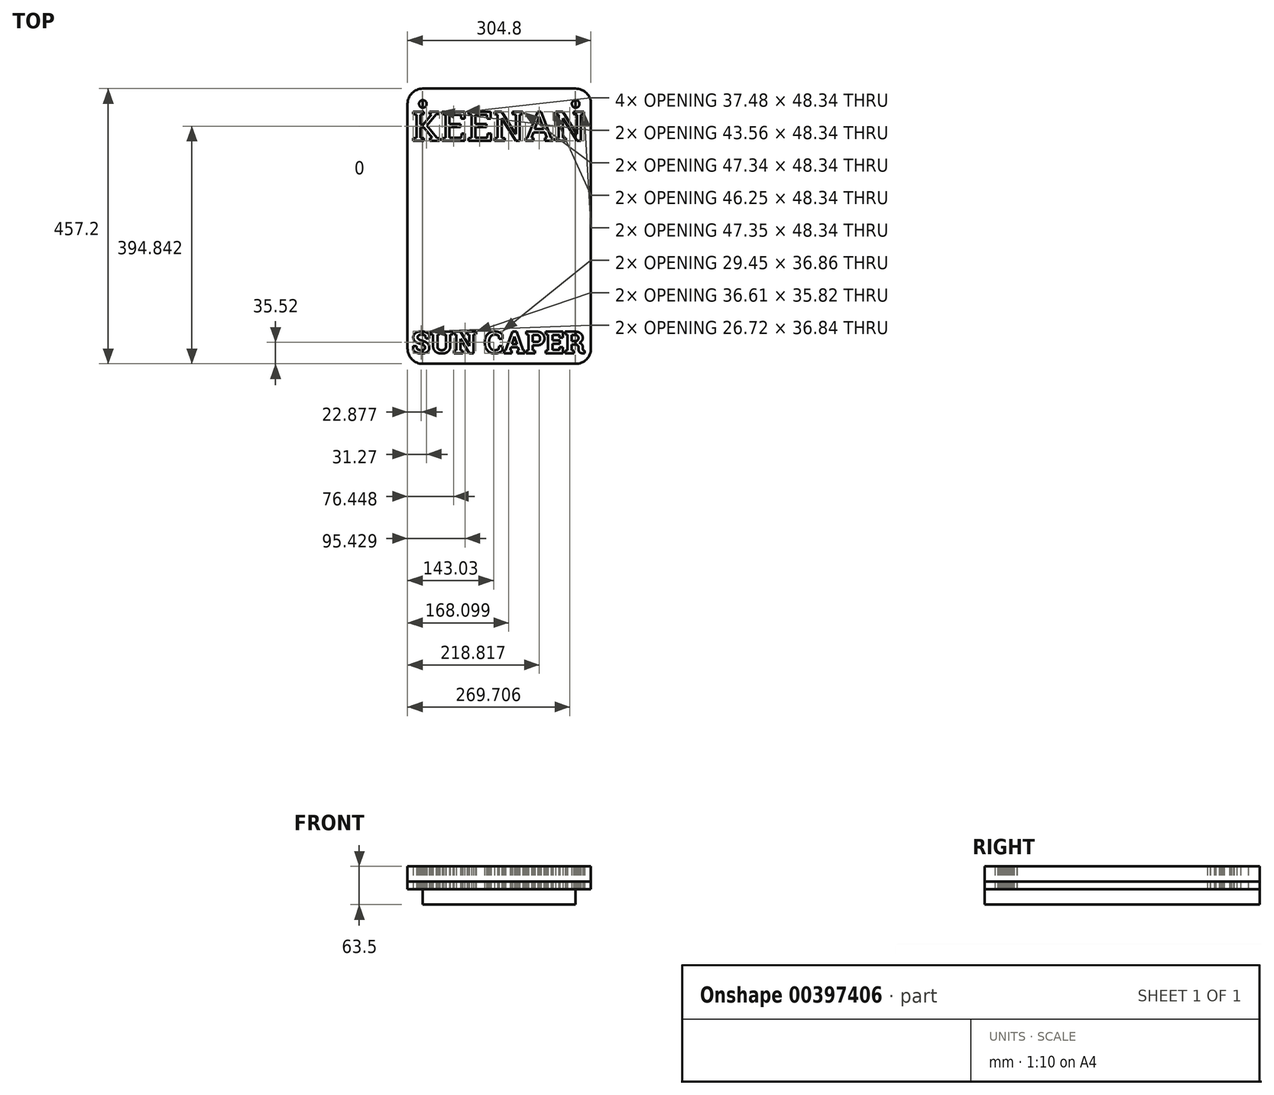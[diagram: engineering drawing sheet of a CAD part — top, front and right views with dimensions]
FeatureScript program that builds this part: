
annotation { "Feature Type Name" : "Feature", "Feature Type Description" : "" }
export const myFeature = defineFeature(function(context is Context, id is Id, definition is map)
    precondition{}
    {
        {
            var Q0;
            Q0=qCreatedBy(makeId("Top.planeOp"),FACE);
            var sketch = newSketch(context, id + "F0", { "sketchPlane" : qUnion([Q0])});
            skLineSegment(sketch, "E0.bottom", {"start": v(25.4, 0) * mm, "end": v(279.4, 0) * mm});
            skLineSegment(sketch, "E0.top", {"start": v(25.4, 457.2) * mm, "end": v(279.4, 457.2) * mm});
            skLineSegment(sketch, "E0.left", {"start": v(0, 25.4) * mm, "end": v(0, 431.8) * mm});
            skLineSegment(sketch, "E0.right", {"start": v(304.8, 25.4) * mm, "end": v(304.8, 431.8) * mm});
            skText(sketch, "E1", { "text": "SUN CAPER", "fontName": "RobotoSlab-Bold.ttf"});
            skText(sketch, "E2", { "text": "KEENAN", "fontName": "RobotoSlab-Regular.ttf"});
            skPoint(sketch, "E3.visualSharp", {"position": v(0, 457.2) * mm});
            skArc(sketch, "E3.filletArc", {"start": v(25.4, 457.2) * mm, "mid": v(7.44, 449.76) * mm, "end": v(0, 431.8) * mm});
            skPoint(sketch, "E4.visualSharp", {"position": v(304.8, 457.2) * mm});
            skArc(sketch, "E4.filletArc", {"start": v(304.8, 431.8) * mm, "mid": v(297.36, 449.76) * mm, "end": v(279.4, 457.2) * mm});
            skPoint(sketch, "E5.visualSharp", {"position": v(304.8, 0) * mm});
            skArc(sketch, "E5.filletArc", {"start": v(279.4, 0) * mm, "mid": v(297.36, 7.44) * mm, "end": v(304.8, 25.4) * mm});
            skPoint(sketch, "E6.visualSharp", {"position": v(0, 0) * mm});
            skArc(sketch, "E6.filletArc", {"start": v(0, 25.4) * mm, "mid": v(7.44, 7.44) * mm, "end": v(25.4, 0) * mm});
            skCircle(sketch, "E7", {"center": v(25.4, 431.8) * mm, "radius": 6.35 * mm});
            skCircle(sketch, "E8", {"center": v(279.4, 431.8) * mm, "radius": 6.35 * mm});
            const initialGuessF0  = {"E1": [0.00713, 0.01762, 1, 0, 0.03628], "E2": [0.00713, 0.37067, 1, 0, 0.04896]};
            skSetInitialGuess(sketch, initialGuessF0);
            skSolve(sketch);
        }
        {
            var Q0;
            Q0=makeQuery(id+"F0.imprint","IMPRINT",FACE,{"disambiguationData":[TD([[makeQuery(id+"F0.imprint","IMPRINT",EDGE,{"derivedFrom":sQuery(id+"F0.wireOp",EDGE,"E0.bottom")}),1.0]])]});
            var Q1;
            Q1=makeQuery(id+"F0.imprint","IMPRINT",FACE,{"disambiguationData":[TD([[makeQuery(id+"F0.imprint","IMPRINT",EDGE,{"derivedFrom":sQuery(id+"F0.wireOp",EDGE,"E2.sketch_text.stroke-109")}),1.0]])]});
            var Q2;
            Q2=makeQuery(id+"F0.imprint","IMPRINT",FACE,{"disambiguationData":[TD([[makeQuery(id+"F0.imprint","IMPRINT",EDGE,{"derivedFrom":sQuery(id+"F0.wireOp",EDGE,"E1.sketch_text.stroke-195")}),1.0]])]});
            var Q3;
            Q3=makeQuery(id+"F0.imprint","IMPRINT",FACE,{"disambiguationData":[TD([[makeQuery(id+"F0.imprint","IMPRINT",EDGE,{"derivedFrom":sQuery(id+"F0.wireOp",EDGE,"E1.sketch_text.stroke-138")}),1.0]])]});
            var Q4;
            Q4=makeQuery(id+"F0.imprint","IMPRINT",FACE,{"disambiguationData":[TD([[makeQuery(id+"F0.imprint","IMPRINT",EDGE,{"derivedFrom":sQuery(id+"F0.wireOp",EDGE,"E1.sketch_text.stroke-118")}),1.0]])]});
            extrude(context, id + "F1", {"entities" : qUnion([Q0, Q1, Q2, Q3, Q4]), "depth" : 25.4 * mm});
        }
        {
            var Q0;
            Q0=makeQuery(id+"F1.opExtrude","CAP_FACE",FACE,{"disambiguationData":[OSD([sQuery(id+"F0.wireOp",EDGE,"E0.bottom"),sQuery(id+"F0.wireOp",EDGE,"E0.top"),sQuery(id+"F0.wireOp",EDGE,"E0.left"),sQuery(id+"F0.wireOp",EDGE,"E0.right"),sQuery(id+"F0.wireOp",EDGE,"E1.sketch_text.stroke-0"),sQuery(id+"F0.wireOp",EDGE,"E1.sketch_text.stroke-1"),sQuery(id+"F0.wireOp",EDGE,"E1.sketch_text.stroke-2"),sQuery(id+"F0.wireOp",EDGE,"E1.sketch_text.stroke-3"),sQuery(id+"F0.wireOp",EDGE,"E1.sketch_text.stroke-4"),sQuery(id+"F0.wireOp",EDGE,"E1.sketch_text.stroke-5"),sQuery(id+"F0.wireOp",EDGE,"E1.sketch_text.stroke-6"),sQuery(id+"F0.wireOp",EDGE,"E1.sketch_text.stroke-7"),sQuery(id+"F0.wireOp",EDGE,"E1.sketch_text.stroke-8"),sQuery(id+"F0.wireOp",EDGE,"E1.sketch_text.stroke-9"),sQuery(id+"F0.wireOp",EDGE,"E1.sketch_text.stroke-10"),sQuery(id+"F0.wireOp",EDGE,"E1.sketch_text.stroke-11"),sQuery(id+"F0.wireOp",EDGE,"E1.sketch_text.stroke-12"),sQuery(id+"F0.wireOp",EDGE,"E1.sketch_text.stroke-13"),sQuery(id+"F0.wireOp",EDGE,"E1.sketch_text.stroke-14"),sQuery(id+"F0.wireOp",EDGE,"E1.sketch_text.stroke-15"),sQuery(id+"F0.wireOp",EDGE,"E1.sketch_text.stroke-16"),sQuery(id+"F0.wireOp",EDGE,"E1.sketch_text.stroke-17"),sQuery(id+"F0.wireOp",EDGE,"E1.sketch_text.stroke-18"),sQuery(id+"F0.wireOp",EDGE,"E1.sketch_text.stroke-19"),sQuery(id+"F0.wireOp",EDGE,"E1.sketch_text.stroke-20"),sQuery(id+"F0.wireOp",EDGE,"E1.sketch_text.stroke-21"),sQuery(id+"F0.wireOp",EDGE,"E1.sketch_text.stroke-22"),sQuery(id+"F0.wireOp",EDGE,"E1.sketch_text.stroke-23"),sQuery(id+"F0.wireOp",EDGE,"E1.sketch_text.stroke-24"),sQuery(id+"F0.wireOp",EDGE,"E1.sketch_text.stroke-25"),sQuery(id+"F0.wireOp",EDGE,"E1.sketch_text.stroke-26"),sQuery(id+"F0.wireOp",EDGE,"E1.sketch_text.stroke-27"),sQuery(id+"F0.wireOp",EDGE,"E1.sketch_text.stroke-28"),sQuery(id+"F0.wireOp",EDGE,"E1.sketch_text.stroke-29"),sQuery(id+"F0.wireOp",EDGE,"E1.sketch_text.stroke-30"),sQuery(id+"F0.wireOp",EDGE,"E1.sketch_text.stroke-31"),sQuery(id+"F0.wireOp",EDGE,"E1.sketch_text.stroke-32"),sQuery(id+"F0.wireOp",EDGE,"E1.sketch_text.stroke-33"),sQuery(id+"F0.wireOp",EDGE,"E1.sketch_text.stroke-34"),sQuery(id+"F0.wireOp",EDGE,"E1.sketch_text.stroke-35"),sQuery(id+"F0.wireOp",EDGE,"E1.sketch_text.stroke-36"),sQuery(id+"F0.wireOp",EDGE,"E1.sketch_text.stroke-37"),sQuery(id+"F0.wireOp",EDGE,"E1.sketch_text.stroke-38"),sQuery(id+"F0.wireOp",EDGE,"E1.sketch_text.stroke-39"),sQuery(id+"F0.wireOp",EDGE,"E1.sketch_text.stroke-40"),sQuery(id+"F0.wireOp",EDGE,"E1.sketch_text.stroke-41"),sQuery(id+"F0.wireOp",EDGE,"E1.sketch_text.stroke-42"),sQuery(id+"F0.wireOp",EDGE,"E1.sketch_text.stroke-43"),sQuery(id+"F0.wireOp",EDGE,"E1.sketch_text.stroke-44"),sQuery(id+"F0.wireOp",EDGE,"E1.sketch_text.stroke-45"),sQuery(id+"F0.wireOp",EDGE,"E1.sketch_text.stroke-46"),sQuery(id+"F0.wireOp",EDGE,"E1.sketch_text.stroke-47"),sQuery(id+"F0.wireOp",EDGE,"E1.sketch_text.stroke-48"),sQuery(id+"F0.wireOp",EDGE,"E1.sketch_text.stroke-49"),sQuery(id+"F0.wireOp",EDGE,"E1.sketch_text.stroke-50"),sQuery(id+"F0.wireOp",EDGE,"E1.sketch_text.stroke-51"),sQuery(id+"F0.wireOp",EDGE,"E1.sketch_text.stroke-52"),sQuery(id+"F0.wireOp",EDGE,"E1.sketch_text.stroke-53"),sQuery(id+"F0.wireOp",EDGE,"E1.sketch_text.stroke-54"),sQuery(id+"F0.wireOp",EDGE,"E1.sketch_text.stroke-55"),sQuery(id+"F0.wireOp",EDGE,"E1.sketch_text.stroke-56"),sQuery(id+"F0.wireOp",EDGE,"E1.sketch_text.stroke-57"),sQuery(id+"F0.wireOp",EDGE,"E1.sketch_text.stroke-58"),sQuery(id+"F0.wireOp",EDGE,"E1.sketch_text.stroke-59"),sQuery(id+"F0.wireOp",EDGE,"E1.sketch_text.stroke-60"),sQuery(id+"F0.wireOp",EDGE,"E1.sketch_text.stroke-61"),sQuery(id+"F0.wireOp",EDGE,"E1.sketch_text.stroke-62"),sQuery(id+"F0.wireOp",EDGE,"E1.sketch_text.stroke-63"),sQuery(id+"F0.wireOp",EDGE,"E1.sketch_text.stroke-64"),sQuery(id+"F0.wireOp",EDGE,"E1.sketch_text.stroke-65"),sQuery(id+"F0.wireOp",EDGE,"E1.sketch_text.stroke-66"),sQuery(id+"F0.wireOp",EDGE,"E1.sketch_text.stroke-67"),sQuery(id+"F0.wireOp",EDGE,"E1.sketch_text.stroke-68"),sQuery(id+"F0.wireOp",EDGE,"E1.sketch_text.stroke-69"),sQuery(id+"F0.wireOp",EDGE,"E1.sketch_text.stroke-70"),sQuery(id+"F0.wireOp",EDGE,"E1.sketch_text.stroke-71"),sQuery(id+"F0.wireOp",EDGE,"E1.sketch_text.stroke-72"),sQuery(id+"F0.wireOp",EDGE,"E1.sketch_text.stroke-73"),sQuery(id+"F0.wireOp",EDGE,"E1.sketch_text.stroke-74"),sQuery(id+"F0.wireOp",EDGE,"E1.sketch_text.stroke-75"),sQuery(id+"F0.wireOp",EDGE,"E1.sketch_text.stroke-76"),sQuery(id+"F0.wireOp",EDGE,"E1.sketch_text.stroke-77"),sQuery(id+"F0.wireOp",EDGE,"E1.sketch_text.stroke-78"),sQuery(id+"F0.wireOp",EDGE,"E1.sketch_text.stroke-79"),sQuery(id+"F0.wireOp",EDGE,"E1.sketch_text.stroke-80"),sQuery(id+"F0.wireOp",EDGE,"E1.sketch_text.stroke-81"),sQuery(id+"F0.wireOp",EDGE,"E1.sketch_text.stroke-82"),sQuery(id+"F0.wireOp",EDGE,"E1.sketch_text.stroke-83"),sQuery(id+"F0.wireOp",EDGE,"E1.sketch_text.stroke-84"),sQuery(id+"F0.wireOp",EDGE,"E1.sketch_text.stroke-85"),sQuery(id+"F0.wireOp",EDGE,"E1.sketch_text.stroke-86"),sQuery(id+"F0.wireOp",EDGE,"E1.sketch_text.stroke-87"),sQuery(id+"F0.wireOp",EDGE,"E1.sketch_text.stroke-88"),sQuery(id+"F0.wireOp",EDGE,"E1.sketch_text.stroke-89"),sQuery(id+"F0.wireOp",EDGE,"E1.sketch_text.stroke-90"),sQuery(id+"F0.wireOp",EDGE,"E1.sketch_text.stroke-91"),sQuery(id+"F0.wireOp",EDGE,"E1.sketch_text.stroke-92"),sQuery(id+"F0.wireOp",EDGE,"E1.sketch_text.stroke-93"),sQuery(id+"F0.wireOp",EDGE,"E1.sketch_text.stroke-94"),sQuery(id+"F0.wireOp",EDGE,"E1.sketch_text.stroke-95"),sQuery(id+"F0.wireOp",EDGE,"E1.sketch_text.stroke-96"),sQuery(id+"F0.wireOp",EDGE,"E1.sketch_text.stroke-97"),sQuery(id+"F0.wireOp",EDGE,"E1.sketch_text.stroke-98"),sQuery(id+"F0.wireOp",EDGE,"E1.sketch_text.stroke-99"),sQuery(id+"F0.wireOp",EDGE,"E1.sketch_text.stroke-100"),sQuery(id+"F0.wireOp",EDGE,"E1.sketch_text.stroke-101"),sQuery(id+"F0.wireOp",EDGE,"E1.sketch_text.stroke-102"),sQuery(id+"F0.wireOp",EDGE,"E1.sketch_text.stroke-103"),sQuery(id+"F0.wireOp",EDGE,"E1.sketch_text.stroke-104"),sQuery(id+"F0.wireOp",EDGE,"E1.sketch_text.stroke-105"),sQuery(id+"F0.wireOp",EDGE,"E1.sketch_text.stroke-106"),sQuery(id+"F0.wireOp",EDGE,"E1.sketch_text.stroke-107"),sQuery(id+"F0.wireOp",EDGE,"E1.sketch_text.stroke-108"),sQuery(id+"F0.wireOp",EDGE,"E1.sketch_text.stroke-109"),sQuery(id+"F0.wireOp",EDGE,"E1.sketch_text.stroke-110"),sQuery(id+"F0.wireOp",EDGE,"E1.sketch_text.stroke-111"),sQuery(id+"F0.wireOp",EDGE,"E1.sketch_text.stroke-112"),sQuery(id+"F0.wireOp",EDGE,"E1.sketch_text.stroke-113"),sQuery(id+"F0.wireOp",EDGE,"E1.sketch_text.stroke-114"),sQuery(id+"F0.wireOp",EDGE,"E1.sketch_text.stroke-115"),sQuery(id+"F0.wireOp",EDGE,"E1.sketch_text.stroke-116"),sQuery(id+"F0.wireOp",EDGE,"E1.sketch_text.stroke-117"),sQuery(id+"F0.wireOp",EDGE,"E1.sketch_text.stroke-122"),sQuery(id+"F0.wireOp",EDGE,"E1.sketch_text.stroke-123"),sQuery(id+"F0.wireOp",EDGE,"E1.sketch_text.stroke-124"),sQuery(id+"F0.wireOp",EDGE,"E1.sketch_text.stroke-125"),sQuery(id+"F0.wireOp",EDGE,"E1.sketch_text.stroke-126"),sQuery(id+"F0.wireOp",EDGE,"E1.sketch_text.stroke-127"),sQuery(id+"F0.wireOp",EDGE,"E1.sketch_text.stroke-128"),sQuery(id+"F0.wireOp",EDGE,"E1.sketch_text.stroke-129"),sQuery(id+"F0.wireOp",EDGE,"E1.sketch_text.stroke-130"),sQuery(id+"F0.wireOp",EDGE,"E1.sketch_text.stroke-131"),sQuery(id+"F0.wireOp",EDGE,"E1.sketch_text.stroke-132"),sQuery(id+"F0.wireOp",EDGE,"E1.sketch_text.stroke-133"),sQuery(id+"F0.wireOp",EDGE,"E1.sketch_text.stroke-134"),sQuery(id+"F0.wireOp",EDGE,"E1.sketch_text.stroke-135"),sQuery(id+"F0.wireOp",EDGE,"E1.sketch_text.stroke-136"),sQuery(id+"F0.wireOp",EDGE,"E1.sketch_text.stroke-137"),sQuery(id+"F0.wireOp",EDGE,"E1.sketch_text.stroke-145"),sQuery(id+"F0.wireOp",EDGE,"E1.sketch_text.stroke-146"),sQuery(id+"F0.wireOp",EDGE,"E1.sketch_text.stroke-147"),sQuery(id+"F0.wireOp",EDGE,"E1.sketch_text.stroke-148"),sQuery(id+"F0.wireOp",EDGE,"E1.sketch_text.stroke-149"),sQuery(id+"F0.wireOp",EDGE,"E1.sketch_text.stroke-150"),sQuery(id+"F0.wireOp",EDGE,"E1.sketch_text.stroke-151"),sQuery(id+"F0.wireOp",EDGE,"E1.sketch_text.stroke-152"),sQuery(id+"F0.wireOp",EDGE,"E1.sketch_text.stroke-153"),sQuery(id+"F0.wireOp",EDGE,"E1.sketch_text.stroke-154"),sQuery(id+"F0.wireOp",EDGE,"E1.sketch_text.stroke-155"),sQuery(id+"F0.wireOp",EDGE,"E1.sketch_text.stroke-156"),sQuery(id+"F0.wireOp",EDGE,"E1.sketch_text.stroke-157"),sQuery(id+"F0.wireOp",EDGE,"E1.sketch_text.stroke-158"),sQuery(id+"F0.wireOp",EDGE,"E1.sketch_text.stroke-159"),sQuery(id+"F0.wireOp",EDGE,"E1.sketch_text.stroke-160"),sQuery(id+"F0.wireOp",EDGE,"E1.sketch_text.stroke-161"),sQuery(id+"F0.wireOp",EDGE,"E1.sketch_text.stroke-162"),sQuery(id+"F0.wireOp",EDGE,"E1.sketch_text.stroke-163"),sQuery(id+"F0.wireOp",EDGE,"E1.sketch_text.stroke-164"),sQuery(id+"F0.wireOp",EDGE,"E1.sketch_text.stroke-165"),sQuery(id+"F0.wireOp",EDGE,"E1.sketch_text.stroke-166"),sQuery(id+"F0.wireOp",EDGE,"E1.sketch_text.stroke-167"),sQuery(id+"F0.wireOp",EDGE,"E1.sketch_text.stroke-168"),sQuery(id+"F0.wireOp",EDGE,"E1.sketch_text.stroke-169"),sQuery(id+"F0.wireOp",EDGE,"E1.sketch_text.stroke-170"),sQuery(id+"F0.wireOp",EDGE,"E1.sketch_text.stroke-171"),sQuery(id+"F0.wireOp",EDGE,"E1.sketch_text.stroke-172"),sQuery(id+"F0.wireOp",EDGE,"E1.sketch_text.stroke-173"),sQuery(id+"F0.wireOp",EDGE,"E1.sketch_text.stroke-174"),sQuery(id+"F0.wireOp",EDGE,"E1.sketch_text.stroke-175"),sQuery(id+"F0.wireOp",EDGE,"E1.sketch_text.stroke-176"),sQuery(id+"F0.wireOp",EDGE,"E1.sketch_text.stroke-177"),sQuery(id+"F0.wireOp",EDGE,"E1.sketch_text.stroke-178"),sQuery(id+"F0.wireOp",EDGE,"E1.sketch_text.stroke-179"),sQuery(id+"F0.wireOp",EDGE,"E1.sketch_text.stroke-180"),sQuery(id+"F0.wireOp",EDGE,"E1.sketch_text.stroke-181"),sQuery(id+"F0.wireOp",EDGE,"E1.sketch_text.stroke-182"),sQuery(id+"F0.wireOp",EDGE,"E1.sketch_text.stroke-183"),sQuery(id+"F0.wireOp",EDGE,"E1.sketch_text.stroke-184"),sQuery(id+"F0.wireOp",EDGE,"E1.sketch_text.stroke-185"),sQuery(id+"F0.wireOp",EDGE,"E1.sketch_text.stroke-186"),sQuery(id+"F0.wireOp",EDGE,"E1.sketch_text.stroke-187"),sQuery(id+"F0.wireOp",EDGE,"E1.sketch_text.stroke-188"),sQuery(id+"F0.wireOp",EDGE,"E1.sketch_text.stroke-189"),sQuery(id+"F0.wireOp",EDGE,"E1.sketch_text.stroke-190"),sQuery(id+"F0.wireOp",EDGE,"E1.sketch_text.stroke-191"),sQuery(id+"F0.wireOp",EDGE,"E1.sketch_text.stroke-192"),sQuery(id+"F0.wireOp",EDGE,"E1.sketch_text.stroke-193"),sQuery(id+"F0.wireOp",EDGE,"E1.sketch_text.stroke-194"),sQuery(id+"F0.wireOp",EDGE,"E2.sketch_text.stroke-0"),sQuery(id+"F0.wireOp",EDGE,"E2.sketch_text.stroke-1"),sQuery(id+"F0.wireOp",EDGE,"E2.sketch_text.stroke-2"),sQuery(id+"F0.wireOp",EDGE,"E2.sketch_text.stroke-3"),sQuery(id+"F0.wireOp",EDGE,"E2.sketch_text.stroke-4"),sQuery(id+"F0.wireOp",EDGE,"E2.sketch_text.stroke-5"),sQuery(id+"F0.wireOp",EDGE,"E2.sketch_text.stroke-6"),sQuery(id+"F0.wireOp",EDGE,"E2.sketch_text.stroke-7"),sQuery(id+"F0.wireOp",EDGE,"E2.sketch_text.stroke-8"),sQuery(id+"F0.wireOp",EDGE,"E2.sketch_text.stroke-9"),sQuery(id+"F0.wireOp",EDGE,"E2.sketch_text.stroke-10"),sQuery(id+"F0.wireOp",EDGE,"E2.sketch_text.stroke-11"),sQuery(id+"F0.wireOp",EDGE,"E2.sketch_text.stroke-12"),sQuery(id+"F0.wireOp",EDGE,"E2.sketch_text.stroke-13"),sQuery(id+"F0.wireOp",EDGE,"E2.sketch_text.stroke-14"),sQuery(id+"F0.wireOp",EDGE,"E2.sketch_text.stroke-15"),sQuery(id+"F0.wireOp",EDGE,"E2.sketch_text.stroke-16"),sQuery(id+"F0.wireOp",EDGE,"E2.sketch_text.stroke-17"),sQuery(id+"F0.wireOp",EDGE,"E2.sketch_text.stroke-18"),sQuery(id+"F0.wireOp",EDGE,"E2.sketch_text.stroke-19"),sQuery(id+"F0.wireOp",EDGE,"E2.sketch_text.stroke-20"),sQuery(id+"F0.wireOp",EDGE,"E2.sketch_text.stroke-21"),sQuery(id+"F0.wireOp",EDGE,"E2.sketch_text.stroke-22"),sQuery(id+"F0.wireOp",EDGE,"E2.sketch_text.stroke-23"),sQuery(id+"F0.wireOp",EDGE,"E2.sketch_text.stroke-24"),sQuery(id+"F0.wireOp",EDGE,"E2.sketch_text.stroke-25"),sQuery(id+"F0.wireOp",EDGE,"E2.sketch_text.stroke-26"),sQuery(id+"F0.wireOp",EDGE,"E2.sketch_text.stroke-27"),sQuery(id+"F0.wireOp",EDGE,"E2.sketch_text.stroke-28"),sQuery(id+"F0.wireOp",EDGE,"E2.sketch_text.stroke-29"),sQuery(id+"F0.wireOp",EDGE,"E2.sketch_text.stroke-30"),sQuery(id+"F0.wireOp",EDGE,"E2.sketch_text.stroke-31"),sQuery(id+"F0.wireOp",EDGE,"E2.sketch_text.stroke-32"),sQuery(id+"F0.wireOp",EDGE,"E2.sketch_text.stroke-33"),sQuery(id+"F0.wireOp",EDGE,"E2.sketch_text.stroke-34"),sQuery(id+"F0.wireOp",EDGE,"E2.sketch_text.stroke-35"),sQuery(id+"F0.wireOp",EDGE,"E2.sketch_text.stroke-36"),sQuery(id+"F0.wireOp",EDGE,"E2.sketch_text.stroke-37"),sQuery(id+"F0.wireOp",EDGE,"E2.sketch_text.stroke-38"),sQuery(id+"F0.wireOp",EDGE,"E2.sketch_text.stroke-39"),sQuery(id+"F0.wireOp",EDGE,"E2.sketch_text.stroke-40"),sQuery(id+"F0.wireOp",EDGE,"E2.sketch_text.stroke-41"),sQuery(id+"F0.wireOp",EDGE,"E2.sketch_text.stroke-42"),sQuery(id+"F0.wireOp",EDGE,"E2.sketch_text.stroke-43"),sQuery(id+"F0.wireOp",EDGE,"E2.sketch_text.stroke-44"),sQuery(id+"F0.wireOp",EDGE,"E2.sketch_text.stroke-45"),sQuery(id+"F0.wireOp",EDGE,"E2.sketch_text.stroke-46"),sQuery(id+"F0.wireOp",EDGE,"E2.sketch_text.stroke-47"),sQuery(id+"F0.wireOp",EDGE,"E2.sketch_text.stroke-48"),sQuery(id+"F0.wireOp",EDGE,"E2.sketch_text.stroke-49"),sQuery(id+"F0.wireOp",EDGE,"E2.sketch_text.stroke-50"),sQuery(id+"F0.wireOp",EDGE,"E2.sketch_text.stroke-51"),sQuery(id+"F0.wireOp",EDGE,"E2.sketch_text.stroke-52"),sQuery(id+"F0.wireOp",EDGE,"E2.sketch_text.stroke-53"),sQuery(id+"F0.wireOp",EDGE,"E2.sketch_text.stroke-54"),sQuery(id+"F0.wireOp",EDGE,"E2.sketch_text.stroke-55"),sQuery(id+"F0.wireOp",EDGE,"E2.sketch_text.stroke-56"),sQuery(id+"F0.wireOp",EDGE,"E2.sketch_text.stroke-57"),sQuery(id+"F0.wireOp",EDGE,"E2.sketch_text.stroke-58"),sQuery(id+"F0.wireOp",EDGE,"E2.sketch_text.stroke-59"),sQuery(id+"F0.wireOp",EDGE,"E2.sketch_text.stroke-60"),sQuery(id+"F0.wireOp",EDGE,"E2.sketch_text.stroke-61"),sQuery(id+"F0.wireOp",EDGE,"E2.sketch_text.stroke-62"),sQuery(id+"F0.wireOp",EDGE,"E2.sketch_text.stroke-63"),sQuery(id+"F0.wireOp",EDGE,"E2.sketch_text.stroke-64"),sQuery(id+"F0.wireOp",EDGE,"E2.sketch_text.stroke-65"),sQuery(id+"F0.wireOp",EDGE,"E2.sketch_text.stroke-66"),sQuery(id+"F0.wireOp",EDGE,"E2.sketch_text.stroke-67"),sQuery(id+"F0.wireOp",EDGE,"E2.sketch_text.stroke-68"),sQuery(id+"F0.wireOp",EDGE,"E2.sketch_text.stroke-69"),sQuery(id+"F0.wireOp",EDGE,"E2.sketch_text.stroke-70"),sQuery(id+"F0.wireOp",EDGE,"E2.sketch_text.stroke-71"),sQuery(id+"F0.wireOp",EDGE,"E2.sketch_text.stroke-72"),sQuery(id+"F0.wireOp",EDGE,"E2.sketch_text.stroke-73"),sQuery(id+"F0.wireOp",EDGE,"E2.sketch_text.stroke-74"),sQuery(id+"F0.wireOp",EDGE,"E2.sketch_text.stroke-75"),sQuery(id+"F0.wireOp",EDGE,"E2.sketch_text.stroke-76"),sQuery(id+"F0.wireOp",EDGE,"E2.sketch_text.stroke-77"),sQuery(id+"F0.wireOp",EDGE,"E2.sketch_text.stroke-78"),sQuery(id+"F0.wireOp",EDGE,"E2.sketch_text.stroke-79"),sQuery(id+"F0.wireOp",EDGE,"E2.sketch_text.stroke-80"),sQuery(id+"F0.wireOp",EDGE,"E2.sketch_text.stroke-81"),sQuery(id+"F0.wireOp",EDGE,"E2.sketch_text.stroke-82"),sQuery(id+"F0.wireOp",EDGE,"E2.sketch_text.stroke-83"),sQuery(id+"F0.wireOp",EDGE,"E2.sketch_text.stroke-84"),sQuery(id+"F0.wireOp",EDGE,"E2.sketch_text.stroke-85"),sQuery(id+"F0.wireOp",EDGE,"E2.sketch_text.stroke-86"),sQuery(id+"F0.wireOp",EDGE,"E2.sketch_text.stroke-87"),sQuery(id+"F0.wireOp",EDGE,"E2.sketch_text.stroke-88"),sQuery(id+"F0.wireOp",EDGE,"E2.sketch_text.stroke-89"),sQuery(id+"F0.wireOp",EDGE,"E2.sketch_text.stroke-90"),sQuery(id+"F0.wireOp",EDGE,"E2.sketch_text.stroke-91"),sQuery(id+"F0.wireOp",EDGE,"E2.sketch_text.stroke-92"),sQuery(id+"F0.wireOp",EDGE,"E2.sketch_text.stroke-93"),sQuery(id+"F0.wireOp",EDGE,"E2.sketch_text.stroke-94"),sQuery(id+"F0.wireOp",EDGE,"E2.sketch_text.stroke-95"),sQuery(id+"F0.wireOp",EDGE,"E2.sketch_text.stroke-96"),sQuery(id+"F0.wireOp",EDGE,"E2.sketch_text.stroke-97"),sQuery(id+"F0.wireOp",EDGE,"E2.sketch_text.stroke-98"),sQuery(id+"F0.wireOp",EDGE,"E2.sketch_text.stroke-99"),sQuery(id+"F0.wireOp",EDGE,"E2.sketch_text.stroke-100"),sQuery(id+"F0.wireOp",EDGE,"E2.sketch_text.stroke-101"),sQuery(id+"F0.wireOp",EDGE,"E2.sketch_text.stroke-102"),sQuery(id+"F0.wireOp",EDGE,"E2.sketch_text.stroke-103"),sQuery(id+"F0.wireOp",EDGE,"E2.sketch_text.stroke-104"),sQuery(id+"F0.wireOp",EDGE,"E2.sketch_text.stroke-105"),sQuery(id+"F0.wireOp",EDGE,"E2.sketch_text.stroke-106"),sQuery(id+"F0.wireOp",EDGE,"E2.sketch_text.stroke-107"),sQuery(id+"F0.wireOp",EDGE,"E2.sketch_text.stroke-108"),sQuery(id+"F0.wireOp",EDGE,"E2.sketch_text.stroke-113"),sQuery(id+"F0.wireOp",EDGE,"E2.sketch_text.stroke-114"),sQuery(id+"F0.wireOp",EDGE,"E2.sketch_text.stroke-115"),sQuery(id+"F0.wireOp",EDGE,"E2.sketch_text.stroke-116"),sQuery(id+"F0.wireOp",EDGE,"E2.sketch_text.stroke-117"),sQuery(id+"F0.wireOp",EDGE,"E2.sketch_text.stroke-118"),sQuery(id+"F0.wireOp",EDGE,"E2.sketch_text.stroke-119"),sQuery(id+"F0.wireOp",EDGE,"E2.sketch_text.stroke-120"),sQuery(id+"F0.wireOp",EDGE,"E2.sketch_text.stroke-121"),sQuery(id+"F0.wireOp",EDGE,"E2.sketch_text.stroke-122"),sQuery(id+"F0.wireOp",EDGE,"E2.sketch_text.stroke-123"),sQuery(id+"F0.wireOp",EDGE,"E2.sketch_text.stroke-124"),sQuery(id+"F0.wireOp",EDGE,"E2.sketch_text.stroke-125"),sQuery(id+"F0.wireOp",EDGE,"E2.sketch_text.stroke-126"),sQuery(id+"F0.wireOp",EDGE,"E2.sketch_text.stroke-127"),sQuery(id+"F0.wireOp",EDGE,"E2.sketch_text.stroke-128"),sQuery(id+"F0.wireOp",EDGE,"E2.sketch_text.stroke-129"),sQuery(id+"F0.wireOp",EDGE,"E2.sketch_text.stroke-130"),sQuery(id+"F0.wireOp",EDGE,"E2.sketch_text.stroke-131"),sQuery(id+"F0.wireOp",EDGE,"E2.sketch_text.stroke-132"),sQuery(id+"F0.wireOp",EDGE,"E2.sketch_text.stroke-133"),sQuery(id+"F0.wireOp",EDGE,"E2.sketch_text.stroke-134"),sQuery(id+"F0.wireOp",EDGE,"E2.sketch_text.stroke-135"),sQuery(id+"F0.wireOp",EDGE,"E2.sketch_text.stroke-136"),sQuery(id+"F0.wireOp",EDGE,"E3.filletArc"),sQuery(id+"F0.wireOp",EDGE,"E4.filletArc"),sQuery(id+"F0.wireOp",EDGE,"E5.filletArc"),sQuery(id+"F0.wireOp",EDGE,"E6.filletArc"),sQuery(id+"F0.wireOp",EDGE,"E7"),sQuery(id+"F0.wireOp",EDGE,"E8")])],"isStart":true});
            var sketch = newSketch(context, id + "F2", { "sketchPlane" : qUnion([Q0])});
            skLineSegment(sketch, "E9.bottom", {"start": v(25.4, 0) * mm, "end": v(279.4, 0) * mm});
            skLineSegment(sketch, "E9.top", {"start": v(25.4, -457.2) * mm, "end": v(279.4, -457.2) * mm});
            skLineSegment(sketch, "E9.left", {"start": v(25.4, 0) * mm, "end": v(25.4, -457.2) * mm});
            skLineSegment(sketch, "E9.right", {"start": v(279.4, 0) * mm, "end": v(279.4, -457.2) * mm});
            skSolve(sketch);
        }
        {
            var Q0;
            Q0 = qSketchRegion(id + "F2", true);
            extrude(context, id + "F3", {"entities" : qUnion([Q0]), "depth" : 25.4 * mm});
        }
        {
            var Q0;
            Q0=makeQuery(id+"F1.opExtrude","CAP_FACE",FACE,{"disambiguationData":[OSD([sQuery(id+"F0.wireOp",EDGE,"E0.bottom"),sQuery(id+"F0.wireOp",EDGE,"E0.top"),sQuery(id+"F0.wireOp",EDGE,"E0.left"),sQuery(id+"F0.wireOp",EDGE,"E0.right"),sQuery(id+"F0.wireOp",EDGE,"E1.sketch_text.stroke-0"),sQuery(id+"F0.wireOp",EDGE,"E1.sketch_text.stroke-1"),sQuery(id+"F0.wireOp",EDGE,"E1.sketch_text.stroke-2"),sQuery(id+"F0.wireOp",EDGE,"E1.sketch_text.stroke-3"),sQuery(id+"F0.wireOp",EDGE,"E1.sketch_text.stroke-4"),sQuery(id+"F0.wireOp",EDGE,"E1.sketch_text.stroke-5"),sQuery(id+"F0.wireOp",EDGE,"E1.sketch_text.stroke-6"),sQuery(id+"F0.wireOp",EDGE,"E1.sketch_text.stroke-7"),sQuery(id+"F0.wireOp",EDGE,"E1.sketch_text.stroke-8"),sQuery(id+"F0.wireOp",EDGE,"E1.sketch_text.stroke-9"),sQuery(id+"F0.wireOp",EDGE,"E1.sketch_text.stroke-10"),sQuery(id+"F0.wireOp",EDGE,"E1.sketch_text.stroke-11"),sQuery(id+"F0.wireOp",EDGE,"E1.sketch_text.stroke-12"),sQuery(id+"F0.wireOp",EDGE,"E1.sketch_text.stroke-13"),sQuery(id+"F0.wireOp",EDGE,"E1.sketch_text.stroke-14"),sQuery(id+"F0.wireOp",EDGE,"E1.sketch_text.stroke-15"),sQuery(id+"F0.wireOp",EDGE,"E1.sketch_text.stroke-16"),sQuery(id+"F0.wireOp",EDGE,"E1.sketch_text.stroke-17"),sQuery(id+"F0.wireOp",EDGE,"E1.sketch_text.stroke-18"),sQuery(id+"F0.wireOp",EDGE,"E1.sketch_text.stroke-19"),sQuery(id+"F0.wireOp",EDGE,"E1.sketch_text.stroke-20"),sQuery(id+"F0.wireOp",EDGE,"E1.sketch_text.stroke-21"),sQuery(id+"F0.wireOp",EDGE,"E1.sketch_text.stroke-22"),sQuery(id+"F0.wireOp",EDGE,"E1.sketch_text.stroke-23"),sQuery(id+"F0.wireOp",EDGE,"E1.sketch_text.stroke-24"),sQuery(id+"F0.wireOp",EDGE,"E1.sketch_text.stroke-25"),sQuery(id+"F0.wireOp",EDGE,"E1.sketch_text.stroke-26"),sQuery(id+"F0.wireOp",EDGE,"E1.sketch_text.stroke-27"),sQuery(id+"F0.wireOp",EDGE,"E1.sketch_text.stroke-28"),sQuery(id+"F0.wireOp",EDGE,"E1.sketch_text.stroke-29"),sQuery(id+"F0.wireOp",EDGE,"E1.sketch_text.stroke-30"),sQuery(id+"F0.wireOp",EDGE,"E1.sketch_text.stroke-31"),sQuery(id+"F0.wireOp",EDGE,"E1.sketch_text.stroke-32"),sQuery(id+"F0.wireOp",EDGE,"E1.sketch_text.stroke-33"),sQuery(id+"F0.wireOp",EDGE,"E1.sketch_text.stroke-34"),sQuery(id+"F0.wireOp",EDGE,"E1.sketch_text.stroke-35"),sQuery(id+"F0.wireOp",EDGE,"E1.sketch_text.stroke-36"),sQuery(id+"F0.wireOp",EDGE,"E1.sketch_text.stroke-37"),sQuery(id+"F0.wireOp",EDGE,"E1.sketch_text.stroke-38"),sQuery(id+"F0.wireOp",EDGE,"E1.sketch_text.stroke-39"),sQuery(id+"F0.wireOp",EDGE,"E1.sketch_text.stroke-40"),sQuery(id+"F0.wireOp",EDGE,"E1.sketch_text.stroke-41"),sQuery(id+"F0.wireOp",EDGE,"E1.sketch_text.stroke-42"),sQuery(id+"F0.wireOp",EDGE,"E1.sketch_text.stroke-43"),sQuery(id+"F0.wireOp",EDGE,"E1.sketch_text.stroke-44"),sQuery(id+"F0.wireOp",EDGE,"E1.sketch_text.stroke-45"),sQuery(id+"F0.wireOp",EDGE,"E1.sketch_text.stroke-46"),sQuery(id+"F0.wireOp",EDGE,"E1.sketch_text.stroke-47"),sQuery(id+"F0.wireOp",EDGE,"E1.sketch_text.stroke-48"),sQuery(id+"F0.wireOp",EDGE,"E1.sketch_text.stroke-49"),sQuery(id+"F0.wireOp",EDGE,"E1.sketch_text.stroke-50"),sQuery(id+"F0.wireOp",EDGE,"E1.sketch_text.stroke-51"),sQuery(id+"F0.wireOp",EDGE,"E1.sketch_text.stroke-52"),sQuery(id+"F0.wireOp",EDGE,"E1.sketch_text.stroke-53"),sQuery(id+"F0.wireOp",EDGE,"E1.sketch_text.stroke-54"),sQuery(id+"F0.wireOp",EDGE,"E1.sketch_text.stroke-55"),sQuery(id+"F0.wireOp",EDGE,"E1.sketch_text.stroke-56"),sQuery(id+"F0.wireOp",EDGE,"E1.sketch_text.stroke-57"),sQuery(id+"F0.wireOp",EDGE,"E1.sketch_text.stroke-58"),sQuery(id+"F0.wireOp",EDGE,"E1.sketch_text.stroke-59"),sQuery(id+"F0.wireOp",EDGE,"E1.sketch_text.stroke-60"),sQuery(id+"F0.wireOp",EDGE,"E1.sketch_text.stroke-61"),sQuery(id+"F0.wireOp",EDGE,"E1.sketch_text.stroke-62"),sQuery(id+"F0.wireOp",EDGE,"E1.sketch_text.stroke-63"),sQuery(id+"F0.wireOp",EDGE,"E1.sketch_text.stroke-64"),sQuery(id+"F0.wireOp",EDGE,"E1.sketch_text.stroke-65"),sQuery(id+"F0.wireOp",EDGE,"E1.sketch_text.stroke-66"),sQuery(id+"F0.wireOp",EDGE,"E1.sketch_text.stroke-67"),sQuery(id+"F0.wireOp",EDGE,"E1.sketch_text.stroke-68"),sQuery(id+"F0.wireOp",EDGE,"E1.sketch_text.stroke-69"),sQuery(id+"F0.wireOp",EDGE,"E1.sketch_text.stroke-70"),sQuery(id+"F0.wireOp",EDGE,"E1.sketch_text.stroke-71"),sQuery(id+"F0.wireOp",EDGE,"E1.sketch_text.stroke-72"),sQuery(id+"F0.wireOp",EDGE,"E1.sketch_text.stroke-73"),sQuery(id+"F0.wireOp",EDGE,"E1.sketch_text.stroke-74"),sQuery(id+"F0.wireOp",EDGE,"E1.sketch_text.stroke-75"),sQuery(id+"F0.wireOp",EDGE,"E1.sketch_text.stroke-76"),sQuery(id+"F0.wireOp",EDGE,"E1.sketch_text.stroke-77"),sQuery(id+"F0.wireOp",EDGE,"E1.sketch_text.stroke-78"),sQuery(id+"F0.wireOp",EDGE,"E1.sketch_text.stroke-79"),sQuery(id+"F0.wireOp",EDGE,"E1.sketch_text.stroke-80"),sQuery(id+"F0.wireOp",EDGE,"E1.sketch_text.stroke-81"),sQuery(id+"F0.wireOp",EDGE,"E1.sketch_text.stroke-82"),sQuery(id+"F0.wireOp",EDGE,"E1.sketch_text.stroke-83"),sQuery(id+"F0.wireOp",EDGE,"E1.sketch_text.stroke-84"),sQuery(id+"F0.wireOp",EDGE,"E1.sketch_text.stroke-85"),sQuery(id+"F0.wireOp",EDGE,"E1.sketch_text.stroke-86"),sQuery(id+"F0.wireOp",EDGE,"E1.sketch_text.stroke-87"),sQuery(id+"F0.wireOp",EDGE,"E1.sketch_text.stroke-88"),sQuery(id+"F0.wireOp",EDGE,"E1.sketch_text.stroke-89"),sQuery(id+"F0.wireOp",EDGE,"E1.sketch_text.stroke-90"),sQuery(id+"F0.wireOp",EDGE,"E1.sketch_text.stroke-91"),sQuery(id+"F0.wireOp",EDGE,"E1.sketch_text.stroke-92"),sQuery(id+"F0.wireOp",EDGE,"E1.sketch_text.stroke-93"),sQuery(id+"F0.wireOp",EDGE,"E1.sketch_text.stroke-94"),sQuery(id+"F0.wireOp",EDGE,"E1.sketch_text.stroke-95"),sQuery(id+"F0.wireOp",EDGE,"E1.sketch_text.stroke-96"),sQuery(id+"F0.wireOp",EDGE,"E1.sketch_text.stroke-97"),sQuery(id+"F0.wireOp",EDGE,"E1.sketch_text.stroke-98"),sQuery(id+"F0.wireOp",EDGE,"E1.sketch_text.stroke-99"),sQuery(id+"F0.wireOp",EDGE,"E1.sketch_text.stroke-100"),sQuery(id+"F0.wireOp",EDGE,"E1.sketch_text.stroke-101"),sQuery(id+"F0.wireOp",EDGE,"E1.sketch_text.stroke-102"),sQuery(id+"F0.wireOp",EDGE,"E1.sketch_text.stroke-103"),sQuery(id+"F0.wireOp",EDGE,"E1.sketch_text.stroke-104"),sQuery(id+"F0.wireOp",EDGE,"E1.sketch_text.stroke-105"),sQuery(id+"F0.wireOp",EDGE,"E1.sketch_text.stroke-106"),sQuery(id+"F0.wireOp",EDGE,"E1.sketch_text.stroke-107"),sQuery(id+"F0.wireOp",EDGE,"E1.sketch_text.stroke-108"),sQuery(id+"F0.wireOp",EDGE,"E1.sketch_text.stroke-109"),sQuery(id+"F0.wireOp",EDGE,"E1.sketch_text.stroke-110"),sQuery(id+"F0.wireOp",EDGE,"E1.sketch_text.stroke-111"),sQuery(id+"F0.wireOp",EDGE,"E1.sketch_text.stroke-112"),sQuery(id+"F0.wireOp",EDGE,"E1.sketch_text.stroke-113"),sQuery(id+"F0.wireOp",EDGE,"E1.sketch_text.stroke-114"),sQuery(id+"F0.wireOp",EDGE,"E1.sketch_text.stroke-115"),sQuery(id+"F0.wireOp",EDGE,"E1.sketch_text.stroke-116"),sQuery(id+"F0.wireOp",EDGE,"E1.sketch_text.stroke-117"),sQuery(id+"F0.wireOp",EDGE,"E1.sketch_text.stroke-122"),sQuery(id+"F0.wireOp",EDGE,"E1.sketch_text.stroke-123"),sQuery(id+"F0.wireOp",EDGE,"E1.sketch_text.stroke-124"),sQuery(id+"F0.wireOp",EDGE,"E1.sketch_text.stroke-125"),sQuery(id+"F0.wireOp",EDGE,"E1.sketch_text.stroke-126"),sQuery(id+"F0.wireOp",EDGE,"E1.sketch_text.stroke-127"),sQuery(id+"F0.wireOp",EDGE,"E1.sketch_text.stroke-128"),sQuery(id+"F0.wireOp",EDGE,"E1.sketch_text.stroke-129"),sQuery(id+"F0.wireOp",EDGE,"E1.sketch_text.stroke-130"),sQuery(id+"F0.wireOp",EDGE,"E1.sketch_text.stroke-131"),sQuery(id+"F0.wireOp",EDGE,"E1.sketch_text.stroke-132"),sQuery(id+"F0.wireOp",EDGE,"E1.sketch_text.stroke-133"),sQuery(id+"F0.wireOp",EDGE,"E1.sketch_text.stroke-134"),sQuery(id+"F0.wireOp",EDGE,"E1.sketch_text.stroke-135"),sQuery(id+"F0.wireOp",EDGE,"E1.sketch_text.stroke-136"),sQuery(id+"F0.wireOp",EDGE,"E1.sketch_text.stroke-137"),sQuery(id+"F0.wireOp",EDGE,"E1.sketch_text.stroke-145"),sQuery(id+"F0.wireOp",EDGE,"E1.sketch_text.stroke-146"),sQuery(id+"F0.wireOp",EDGE,"E1.sketch_text.stroke-147"),sQuery(id+"F0.wireOp",EDGE,"E1.sketch_text.stroke-148"),sQuery(id+"F0.wireOp",EDGE,"E1.sketch_text.stroke-149"),sQuery(id+"F0.wireOp",EDGE,"E1.sketch_text.stroke-150"),sQuery(id+"F0.wireOp",EDGE,"E1.sketch_text.stroke-151"),sQuery(id+"F0.wireOp",EDGE,"E1.sketch_text.stroke-152"),sQuery(id+"F0.wireOp",EDGE,"E1.sketch_text.stroke-153"),sQuery(id+"F0.wireOp",EDGE,"E1.sketch_text.stroke-154"),sQuery(id+"F0.wireOp",EDGE,"E1.sketch_text.stroke-155"),sQuery(id+"F0.wireOp",EDGE,"E1.sketch_text.stroke-156"),sQuery(id+"F0.wireOp",EDGE,"E1.sketch_text.stroke-157"),sQuery(id+"F0.wireOp",EDGE,"E1.sketch_text.stroke-158"),sQuery(id+"F0.wireOp",EDGE,"E1.sketch_text.stroke-159"),sQuery(id+"F0.wireOp",EDGE,"E1.sketch_text.stroke-160"),sQuery(id+"F0.wireOp",EDGE,"E1.sketch_text.stroke-161"),sQuery(id+"F0.wireOp",EDGE,"E1.sketch_text.stroke-162"),sQuery(id+"F0.wireOp",EDGE,"E1.sketch_text.stroke-163"),sQuery(id+"F0.wireOp",EDGE,"E1.sketch_text.stroke-164"),sQuery(id+"F0.wireOp",EDGE,"E1.sketch_text.stroke-165"),sQuery(id+"F0.wireOp",EDGE,"E1.sketch_text.stroke-166"),sQuery(id+"F0.wireOp",EDGE,"E1.sketch_text.stroke-167"),sQuery(id+"F0.wireOp",EDGE,"E1.sketch_text.stroke-168"),sQuery(id+"F0.wireOp",EDGE,"E1.sketch_text.stroke-169"),sQuery(id+"F0.wireOp",EDGE,"E1.sketch_text.stroke-170"),sQuery(id+"F0.wireOp",EDGE,"E1.sketch_text.stroke-171"),sQuery(id+"F0.wireOp",EDGE,"E1.sketch_text.stroke-172"),sQuery(id+"F0.wireOp",EDGE,"E1.sketch_text.stroke-173"),sQuery(id+"F0.wireOp",EDGE,"E1.sketch_text.stroke-174"),sQuery(id+"F0.wireOp",EDGE,"E1.sketch_text.stroke-175"),sQuery(id+"F0.wireOp",EDGE,"E1.sketch_text.stroke-176"),sQuery(id+"F0.wireOp",EDGE,"E1.sketch_text.stroke-177"),sQuery(id+"F0.wireOp",EDGE,"E1.sketch_text.stroke-178"),sQuery(id+"F0.wireOp",EDGE,"E1.sketch_text.stroke-179"),sQuery(id+"F0.wireOp",EDGE,"E1.sketch_text.stroke-180"),sQuery(id+"F0.wireOp",EDGE,"E1.sketch_text.stroke-181"),sQuery(id+"F0.wireOp",EDGE,"E1.sketch_text.stroke-182"),sQuery(id+"F0.wireOp",EDGE,"E1.sketch_text.stroke-183"),sQuery(id+"F0.wireOp",EDGE,"E1.sketch_text.stroke-184"),sQuery(id+"F0.wireOp",EDGE,"E1.sketch_text.stroke-185"),sQuery(id+"F0.wireOp",EDGE,"E1.sketch_text.stroke-186"),sQuery(id+"F0.wireOp",EDGE,"E1.sketch_text.stroke-187"),sQuery(id+"F0.wireOp",EDGE,"E1.sketch_text.stroke-188"),sQuery(id+"F0.wireOp",EDGE,"E1.sketch_text.stroke-189"),sQuery(id+"F0.wireOp",EDGE,"E1.sketch_text.stroke-190"),sQuery(id+"F0.wireOp",EDGE,"E1.sketch_text.stroke-191"),sQuery(id+"F0.wireOp",EDGE,"E1.sketch_text.stroke-192"),sQuery(id+"F0.wireOp",EDGE,"E1.sketch_text.stroke-193"),sQuery(id+"F0.wireOp",EDGE,"E1.sketch_text.stroke-194"),sQuery(id+"F0.wireOp",EDGE,"E2.sketch_text.stroke-0"),sQuery(id+"F0.wireOp",EDGE,"E2.sketch_text.stroke-1"),sQuery(id+"F0.wireOp",EDGE,"E2.sketch_text.stroke-2"),sQuery(id+"F0.wireOp",EDGE,"E2.sketch_text.stroke-3"),sQuery(id+"F0.wireOp",EDGE,"E2.sketch_text.stroke-4"),sQuery(id+"F0.wireOp",EDGE,"E2.sketch_text.stroke-5"),sQuery(id+"F0.wireOp",EDGE,"E2.sketch_text.stroke-6"),sQuery(id+"F0.wireOp",EDGE,"E2.sketch_text.stroke-7"),sQuery(id+"F0.wireOp",EDGE,"E2.sketch_text.stroke-8"),sQuery(id+"F0.wireOp",EDGE,"E2.sketch_text.stroke-9"),sQuery(id+"F0.wireOp",EDGE,"E2.sketch_text.stroke-10"),sQuery(id+"F0.wireOp",EDGE,"E2.sketch_text.stroke-11"),sQuery(id+"F0.wireOp",EDGE,"E2.sketch_text.stroke-12"),sQuery(id+"F0.wireOp",EDGE,"E2.sketch_text.stroke-13"),sQuery(id+"F0.wireOp",EDGE,"E2.sketch_text.stroke-14"),sQuery(id+"F0.wireOp",EDGE,"E2.sketch_text.stroke-15"),sQuery(id+"F0.wireOp",EDGE,"E2.sketch_text.stroke-16"),sQuery(id+"F0.wireOp",EDGE,"E2.sketch_text.stroke-17"),sQuery(id+"F0.wireOp",EDGE,"E2.sketch_text.stroke-18"),sQuery(id+"F0.wireOp",EDGE,"E2.sketch_text.stroke-19"),sQuery(id+"F0.wireOp",EDGE,"E2.sketch_text.stroke-20"),sQuery(id+"F0.wireOp",EDGE,"E2.sketch_text.stroke-21"),sQuery(id+"F0.wireOp",EDGE,"E2.sketch_text.stroke-22"),sQuery(id+"F0.wireOp",EDGE,"E2.sketch_text.stroke-23"),sQuery(id+"F0.wireOp",EDGE,"E2.sketch_text.stroke-24"),sQuery(id+"F0.wireOp",EDGE,"E2.sketch_text.stroke-25"),sQuery(id+"F0.wireOp",EDGE,"E2.sketch_text.stroke-26"),sQuery(id+"F0.wireOp",EDGE,"E2.sketch_text.stroke-27"),sQuery(id+"F0.wireOp",EDGE,"E2.sketch_text.stroke-28"),sQuery(id+"F0.wireOp",EDGE,"E2.sketch_text.stroke-29"),sQuery(id+"F0.wireOp",EDGE,"E2.sketch_text.stroke-30"),sQuery(id+"F0.wireOp",EDGE,"E2.sketch_text.stroke-31"),sQuery(id+"F0.wireOp",EDGE,"E2.sketch_text.stroke-32"),sQuery(id+"F0.wireOp",EDGE,"E2.sketch_text.stroke-33"),sQuery(id+"F0.wireOp",EDGE,"E2.sketch_text.stroke-34"),sQuery(id+"F0.wireOp",EDGE,"E2.sketch_text.stroke-35"),sQuery(id+"F0.wireOp",EDGE,"E2.sketch_text.stroke-36"),sQuery(id+"F0.wireOp",EDGE,"E2.sketch_text.stroke-37"),sQuery(id+"F0.wireOp",EDGE,"E2.sketch_text.stroke-38"),sQuery(id+"F0.wireOp",EDGE,"E2.sketch_text.stroke-39"),sQuery(id+"F0.wireOp",EDGE,"E2.sketch_text.stroke-40"),sQuery(id+"F0.wireOp",EDGE,"E2.sketch_text.stroke-41"),sQuery(id+"F0.wireOp",EDGE,"E2.sketch_text.stroke-42"),sQuery(id+"F0.wireOp",EDGE,"E2.sketch_text.stroke-43"),sQuery(id+"F0.wireOp",EDGE,"E2.sketch_text.stroke-44"),sQuery(id+"F0.wireOp",EDGE,"E2.sketch_text.stroke-45"),sQuery(id+"F0.wireOp",EDGE,"E2.sketch_text.stroke-46"),sQuery(id+"F0.wireOp",EDGE,"E2.sketch_text.stroke-47"),sQuery(id+"F0.wireOp",EDGE,"E2.sketch_text.stroke-48"),sQuery(id+"F0.wireOp",EDGE,"E2.sketch_text.stroke-49"),sQuery(id+"F0.wireOp",EDGE,"E2.sketch_text.stroke-50"),sQuery(id+"F0.wireOp",EDGE,"E2.sketch_text.stroke-51"),sQuery(id+"F0.wireOp",EDGE,"E2.sketch_text.stroke-52"),sQuery(id+"F0.wireOp",EDGE,"E2.sketch_text.stroke-53"),sQuery(id+"F0.wireOp",EDGE,"E2.sketch_text.stroke-54"),sQuery(id+"F0.wireOp",EDGE,"E2.sketch_text.stroke-55"),sQuery(id+"F0.wireOp",EDGE,"E2.sketch_text.stroke-56"),sQuery(id+"F0.wireOp",EDGE,"E2.sketch_text.stroke-57"),sQuery(id+"F0.wireOp",EDGE,"E2.sketch_text.stroke-58"),sQuery(id+"F0.wireOp",EDGE,"E2.sketch_text.stroke-59"),sQuery(id+"F0.wireOp",EDGE,"E2.sketch_text.stroke-60"),sQuery(id+"F0.wireOp",EDGE,"E2.sketch_text.stroke-61"),sQuery(id+"F0.wireOp",EDGE,"E2.sketch_text.stroke-62"),sQuery(id+"F0.wireOp",EDGE,"E2.sketch_text.stroke-63"),sQuery(id+"F0.wireOp",EDGE,"E2.sketch_text.stroke-64"),sQuery(id+"F0.wireOp",EDGE,"E2.sketch_text.stroke-65"),sQuery(id+"F0.wireOp",EDGE,"E2.sketch_text.stroke-66"),sQuery(id+"F0.wireOp",EDGE,"E2.sketch_text.stroke-67"),sQuery(id+"F0.wireOp",EDGE,"E2.sketch_text.stroke-68"),sQuery(id+"F0.wireOp",EDGE,"E2.sketch_text.stroke-69"),sQuery(id+"F0.wireOp",EDGE,"E2.sketch_text.stroke-70"),sQuery(id+"F0.wireOp",EDGE,"E2.sketch_text.stroke-71"),sQuery(id+"F0.wireOp",EDGE,"E2.sketch_text.stroke-72"),sQuery(id+"F0.wireOp",EDGE,"E2.sketch_text.stroke-73"),sQuery(id+"F0.wireOp",EDGE,"E2.sketch_text.stroke-74"),sQuery(id+"F0.wireOp",EDGE,"E2.sketch_text.stroke-75"),sQuery(id+"F0.wireOp",EDGE,"E2.sketch_text.stroke-76"),sQuery(id+"F0.wireOp",EDGE,"E2.sketch_text.stroke-77"),sQuery(id+"F0.wireOp",EDGE,"E2.sketch_text.stroke-78"),sQuery(id+"F0.wireOp",EDGE,"E2.sketch_text.stroke-79"),sQuery(id+"F0.wireOp",EDGE,"E2.sketch_text.stroke-80"),sQuery(id+"F0.wireOp",EDGE,"E2.sketch_text.stroke-81"),sQuery(id+"F0.wireOp",EDGE,"E2.sketch_text.stroke-82"),sQuery(id+"F0.wireOp",EDGE,"E2.sketch_text.stroke-83"),sQuery(id+"F0.wireOp",EDGE,"E2.sketch_text.stroke-84"),sQuery(id+"F0.wireOp",EDGE,"E2.sketch_text.stroke-85"),sQuery(id+"F0.wireOp",EDGE,"E2.sketch_text.stroke-86"),sQuery(id+"F0.wireOp",EDGE,"E2.sketch_text.stroke-87"),sQuery(id+"F0.wireOp",EDGE,"E2.sketch_text.stroke-88"),sQuery(id+"F0.wireOp",EDGE,"E2.sketch_text.stroke-89"),sQuery(id+"F0.wireOp",EDGE,"E2.sketch_text.stroke-90"),sQuery(id+"F0.wireOp",EDGE,"E2.sketch_text.stroke-91"),sQuery(id+"F0.wireOp",EDGE,"E2.sketch_text.stroke-92"),sQuery(id+"F0.wireOp",EDGE,"E2.sketch_text.stroke-93"),sQuery(id+"F0.wireOp",EDGE,"E2.sketch_text.stroke-94"),sQuery(id+"F0.wireOp",EDGE,"E2.sketch_text.stroke-95"),sQuery(id+"F0.wireOp",EDGE,"E2.sketch_text.stroke-96"),sQuery(id+"F0.wireOp",EDGE,"E2.sketch_text.stroke-97"),sQuery(id+"F0.wireOp",EDGE,"E2.sketch_text.stroke-98"),sQuery(id+"F0.wireOp",EDGE,"E2.sketch_text.stroke-99"),sQuery(id+"F0.wireOp",EDGE,"E2.sketch_text.stroke-100"),sQuery(id+"F0.wireOp",EDGE,"E2.sketch_text.stroke-101"),sQuery(id+"F0.wireOp",EDGE,"E2.sketch_text.stroke-102"),sQuery(id+"F0.wireOp",EDGE,"E2.sketch_text.stroke-103"),sQuery(id+"F0.wireOp",EDGE,"E2.sketch_text.stroke-104"),sQuery(id+"F0.wireOp",EDGE,"E2.sketch_text.stroke-105"),sQuery(id+"F0.wireOp",EDGE,"E2.sketch_text.stroke-106"),sQuery(id+"F0.wireOp",EDGE,"E2.sketch_text.stroke-107"),sQuery(id+"F0.wireOp",EDGE,"E2.sketch_text.stroke-108"),sQuery(id+"F0.wireOp",EDGE,"E2.sketch_text.stroke-113"),sQuery(id+"F0.wireOp",EDGE,"E2.sketch_text.stroke-114"),sQuery(id+"F0.wireOp",EDGE,"E2.sketch_text.stroke-115"),sQuery(id+"F0.wireOp",EDGE,"E2.sketch_text.stroke-116"),sQuery(id+"F0.wireOp",EDGE,"E2.sketch_text.stroke-117"),sQuery(id+"F0.wireOp",EDGE,"E2.sketch_text.stroke-118"),sQuery(id+"F0.wireOp",EDGE,"E2.sketch_text.stroke-119"),sQuery(id+"F0.wireOp",EDGE,"E2.sketch_text.stroke-120"),sQuery(id+"F0.wireOp",EDGE,"E2.sketch_text.stroke-121"),sQuery(id+"F0.wireOp",EDGE,"E2.sketch_text.stroke-122"),sQuery(id+"F0.wireOp",EDGE,"E2.sketch_text.stroke-123"),sQuery(id+"F0.wireOp",EDGE,"E2.sketch_text.stroke-124"),sQuery(id+"F0.wireOp",EDGE,"E2.sketch_text.stroke-125"),sQuery(id+"F0.wireOp",EDGE,"E2.sketch_text.stroke-126"),sQuery(id+"F0.wireOp",EDGE,"E2.sketch_text.stroke-127"),sQuery(id+"F0.wireOp",EDGE,"E2.sketch_text.stroke-128"),sQuery(id+"F0.wireOp",EDGE,"E2.sketch_text.stroke-129"),sQuery(id+"F0.wireOp",EDGE,"E2.sketch_text.stroke-130"),sQuery(id+"F0.wireOp",EDGE,"E2.sketch_text.stroke-131"),sQuery(id+"F0.wireOp",EDGE,"E2.sketch_text.stroke-132"),sQuery(id+"F0.wireOp",EDGE,"E2.sketch_text.stroke-133"),sQuery(id+"F0.wireOp",EDGE,"E2.sketch_text.stroke-134"),sQuery(id+"F0.wireOp",EDGE,"E2.sketch_text.stroke-135"),sQuery(id+"F0.wireOp",EDGE,"E2.sketch_text.stroke-136"),sQuery(id+"F0.wireOp",EDGE,"E3.filletArc"),sQuery(id+"F0.wireOp",EDGE,"E4.filletArc"),sQuery(id+"F0.wireOp",EDGE,"E5.filletArc"),sQuery(id+"F0.wireOp",EDGE,"E6.filletArc"),sQuery(id+"F0.wireOp",EDGE,"E7"),sQuery(id+"F0.wireOp",EDGE,"E8")])],"isStart":false});
            var sketch = newSketch(context, id + "F4", { "sketchPlane" : qUnion([Q0])});
            skLineSegment(sketch, "E10.bottom", {"start": v(-52.38, 469.7) * mm, "end": v(397, 469.7) * mm});
            skLineSegment(sketch, "E10.top", {"start": v(-52.38, -38.93) * mm, "end": v(397, -38.93) * mm});
            skLineSegment(sketch, "E10.left", {"start": v(-52.38, 469.7) * mm, "end": v(-52.38, -38.93) * mm});
            skLineSegment(sketch, "E10.right", {"start": v(397, 469.7) * mm, "end": v(397, -38.93) * mm});
            skSolve(sketch);
        }
        {
            var Q0;
            Q0 = qSketchRegion(id + "F4", true);
            extrude(context, id + "F5", {"entities" : qUnion([Q0]), "operationType" : NewBodyOperationType.REMOVE, "oppositeDirection" : true, "depth" : 12.7 * mm});
        }
        {
            var Q0;
            Q0=makeQuery(id+"F5.boolean.opBoolean","COPY",FACE,{"disambiguationData":[TD([makeQuery(id+"F1.opExtrude","SWEPT_FACE",FACE,{"disambiguationData":[OSD([sQuery(id+"F0.wireOp",EDGE,"E0.bottom")])]})])],"derivedFrom":makeQuery(id+"F5.opExtrude","CAP_FACE",FACE,{"disambiguationData":[OSD([sQuery(id+"F4.wireOp",EDGE,"E10.bottom"),sQuery(id+"F4.wireOp",EDGE,"E10.top"),sQuery(id+"F4.wireOp",EDGE,"E10.left"),sQuery(id+"F4.wireOp",EDGE,"E10.right")])],"isStart":false})});
            var Q1;
            Q1=makeQuery(id+"F5.boolean.opBoolean","COPY",FACE,{"disambiguationData":[TD([makeQuery(id+"F1.opExtrude","SWEPT_FACE",FACE,{"disambiguationData":[OSD([sQuery(id+"F0.wireOp",EDGE,"E1.sketch_text.stroke-138")])]})])],"derivedFrom":makeQuery(id+"F5.opExtrude","CAP_FACE",FACE,{"disambiguationData":[OSD([sQuery(id+"F4.wireOp",EDGE,"E10.bottom"),sQuery(id+"F4.wireOp",EDGE,"E10.top"),sQuery(id+"F4.wireOp",EDGE,"E10.left"),sQuery(id+"F4.wireOp",EDGE,"E10.right")])],"isStart":false})});
            var Q2;
            Q2=makeQuery(id+"F5.boolean.opBoolean","COPY",FACE,{"disambiguationData":[TD([makeQuery(id+"F1.opExtrude","SWEPT_FACE",FACE,{"disambiguationData":[OSD([sQuery(id+"F0.wireOp",EDGE,"E1.sketch_text.stroke-118")])]})])],"derivedFrom":makeQuery(id+"F5.opExtrude","CAP_FACE",FACE,{"disambiguationData":[OSD([sQuery(id+"F4.wireOp",EDGE,"E10.bottom"),sQuery(id+"F4.wireOp",EDGE,"E10.top"),sQuery(id+"F4.wireOp",EDGE,"E10.left"),sQuery(id+"F4.wireOp",EDGE,"E10.right")])],"isStart":false})});
            var Q3;
            Q3=makeQuery(id+"F5.boolean.opBoolean","COPY",FACE,{"disambiguationData":[TD([makeQuery(id+"F1.opExtrude","SWEPT_FACE",FACE,{"disambiguationData":[OSD([sQuery(id+"F0.wireOp",EDGE,"E1.sketch_text.stroke-195")])]})])],"derivedFrom":makeQuery(id+"F5.opExtrude","CAP_FACE",FACE,{"disambiguationData":[OSD([sQuery(id+"F4.wireOp",EDGE,"E10.bottom"),sQuery(id+"F4.wireOp",EDGE,"E10.top"),sQuery(id+"F4.wireOp",EDGE,"E10.left"),sQuery(id+"F4.wireOp",EDGE,"E10.right")])],"isStart":false})});
            var Q4;
            Q4=makeQuery(id+"F5.boolean.opBoolean","COPY",FACE,{"disambiguationData":[TD([makeQuery(id+"F1.opExtrude","SWEPT_FACE",FACE,{"disambiguationData":[OSD([sQuery(id+"F0.wireOp",EDGE,"E2.sketch_text.stroke-109")])]})])],"derivedFrom":makeQuery(id+"F5.opExtrude","CAP_FACE",FACE,{"disambiguationData":[OSD([sQuery(id+"F4.wireOp",EDGE,"E10.bottom"),sQuery(id+"F4.wireOp",EDGE,"E10.top"),sQuery(id+"F4.wireOp",EDGE,"E10.left"),sQuery(id+"F4.wireOp",EDGE,"E10.right")])],"isStart":false})});
            extrude(context, id + "F6", {"entities" : qUnion([Q0, Q1, Q2, Q3, Q4]), "depth" : 25.4 * mm});
        }
    });
